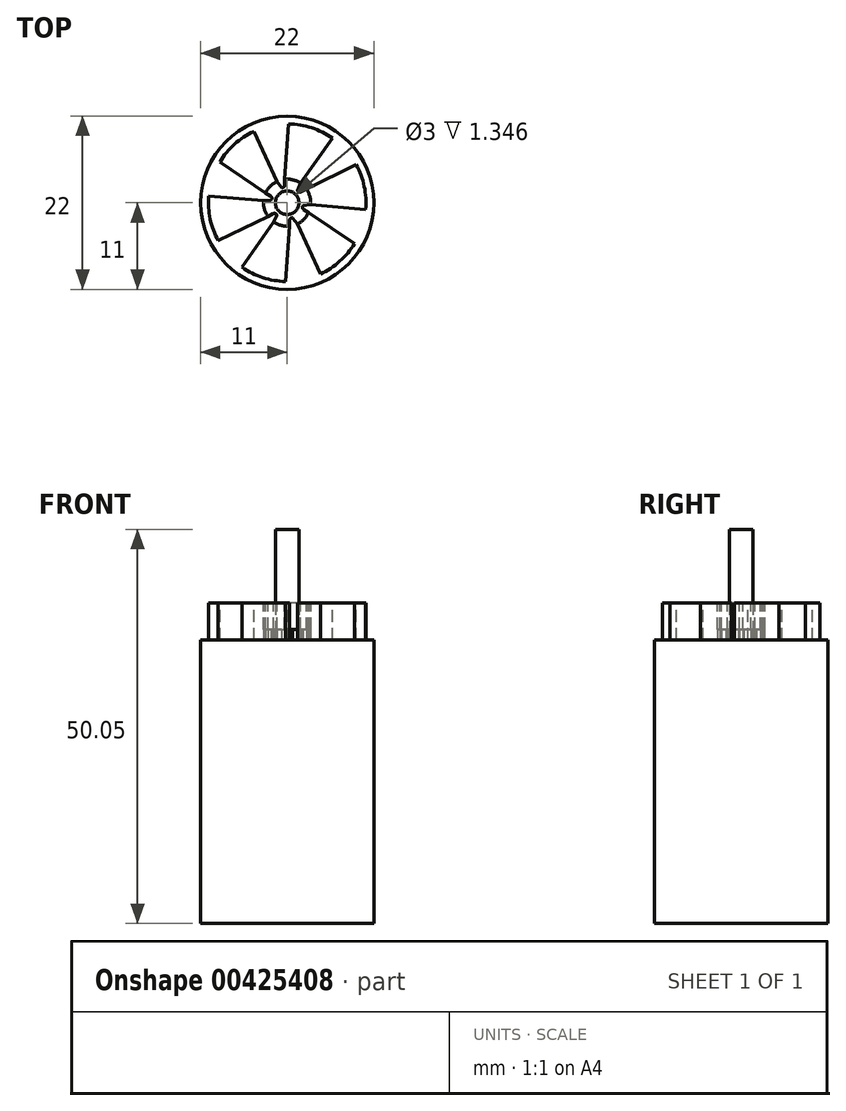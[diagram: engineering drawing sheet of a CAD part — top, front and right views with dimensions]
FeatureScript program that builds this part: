
annotation { "Feature Type Name" : "Feature", "Feature Type Description" : "" }
export const myFeature = defineFeature(function(context is Context, id is Id, definition is map)
    precondition{}
    {
        {
            var Q0;
            Q0=qCreatedBy(makeId("Top.planeOp"),FACE);
            var sketch = newSketch(context, id + "F0", { "sketchPlane" : qUnion([Q0])});
            skCircle(sketch, "E0", {"center": v(0, 0) * mm, "radius": 11 * mm});
            skSolve(sketch);
        }
        {
            var Q0;
            Q0=makeQuery(id+"F0.imprint","IMPRINT",FACE,{"disambiguationData":[TD([[makeQuery(id+"F0.imprint","IMPRINT",EDGE,{"derivedFrom":sQuery(id+"F0.wireOp",EDGE,"E0")}),1.0]])]});
            extrude(context, id + "F1", {"entities" : qUnion([Q0]), "depth" : 36 * mm});
        }
        {
            var Q0;
            Q0=makeQuery(id+"F1.opExtrude","CAP_FACE",FACE,{"disambiguationData":[OSD([sQuery(id+"F0.wireOp",EDGE,"E0")])],"isStart":false});
            var sketch = newSketch(context, id + "F2", { "sketchPlane" : qUnion([Q0])});
            skCircle(sketch, "E1", {"center": v(0, 0) * mm, "radius": 10 * mm});
            skCircle(sketch, "E2", {"center": v(0, 0) * mm, "radius": 1.5 * mm});
            skLineSegment(sketch, "E3", {"start": v(-0.3, 2.98) * mm, "end": v(-0.3, 2.25) * mm});
            skArc(sketch, "E4", {"start": v(-0.3, 2.25) * mm, "mid": v(-0.43, 2) * mm, "end": v(-0.7, 1.92) * mm});
            skLineSegment(sketch, "E5", {"start": v(-0.7, 1.92) * mm, "end": v(-1.29, 2.71) * mm});
            skLineSegment(sketch, "E6.1.0", {"start": v(-2.02, 0.35) * mm, "end": v(-3, 0.24) * mm});
            skArc(sketch, "E6.1.1", {"start": v(-2.1, 0.86) * mm, "mid": v(-1.94, 0.63) * mm, "end": v(-2.02, 0.35) * mm});
            skLineSegment(sketch, "E6.1.2", {"start": v(-2.74, 1.23) * mm, "end": v(-2.1, 0.86) * mm});
            skCircle(sketch, "E6.1.3", {"center": v(0, 0) * mm, "radius": 3 * mm});
            skLineSegment(sketch, "E6.2.0", {"start": v(-1.31, -1.57) * mm, "end": v(-1.7, -2.47) * mm});
            skArc(sketch, "E6.2.1", {"start": v(-1.8, -1.4) * mm, "mid": v(-1.51, -1.37) * mm, "end": v(-1.31, -1.57) * mm});
            skLineSegment(sketch, "E6.2.2", {"start": v(-2.43, -1.76) * mm, "end": v(-1.8, -1.4) * mm});
            skLineSegment(sketch, "E6.3.0", {"start": v(0.7, -1.92) * mm, "end": v(1.29, -2.71) * mm});
            skArc(sketch, "E6.3.1", {"start": v(0.3, -2.25) * mm, "mid": v(0.43, -2) * mm, "end": v(0.7, -1.92) * mm});
            skLineSegment(sketch, "E6.3.2", {"start": v(0.3, -2.98) * mm, "end": v(0.3, -2.25) * mm});
            skLineSegment(sketch, "E6.4.0", {"start": v(2.02, -0.35) * mm, "end": v(3, -0.24) * mm});
            skArc(sketch, "E6.4.1", {"start": v(2.1, -0.86) * mm, "mid": v(1.94, -0.63) * mm, "end": v(2.02, -0.35) * mm});
            skLineSegment(sketch, "E6.4.2", {"start": v(2.74, -1.23) * mm, "end": v(2.1, -0.86) * mm});
            skLineSegment(sketch, "E6.5.0", {"start": v(1.31, 1.57) * mm, "end": v(1.7, 2.47) * mm});
            skArc(sketch, "E6.5.1", {"start": v(1.8, 1.4) * mm, "mid": v(1.51, 1.37) * mm, "end": v(1.31, 1.57) * mm});
            skLineSegment(sketch, "E6.5.2", {"start": v(2.43, 1.76) * mm, "end": v(1.8, 1.4) * mm});
            skArc(sketch, "E7.trimOffspring", {"start": v(-2.43, -1.76) * mm, "mid": v(2.93, -0.63) * mm, "end": v(-1.5, 2.6) * mm});
            skSolve(sketch);
        }
        {
            var Q0;
            Q0=makeQuery(id+"F2.imprint","IMPRINT",FACE,{"disambiguationData":[TD([[makeQuery(id+"F2.imprint","IMPRINT",EDGE,{"derivedFrom":sQuery(id+"F2.wireOp",EDGE,"E2")}),-1.0]])]});
            extrude(context, id + "F3", {"entities" : qUnion([Q0]), "operationType" : NewBodyOperationType.ADD, "depth" : 1.35 * mm});
        }
        {
            var Q0;
            Q0=makeQuery(id+"F3.opExtrude","CAP_FACE",FACE,{"disambiguationData":[OSD([sQuery(id+"F2.wireOp",EDGE,"E2"),sQuery(id+"F2.wireOp",EDGE,"E3"),sQuery(id+"F2.wireOp",EDGE,"E4"),sQuery(id+"F2.wireOp",EDGE,"E5"),sQuery(id+"F2.wireOp",EDGE,"E6.1.0"),sQuery(id+"F2.wireOp",EDGE,"E6.1.1"),sQuery(id+"F2.wireOp",EDGE,"E6.1.2"),sQuery(id+"F2.wireOp",EDGE,"E6.1.3"),sQuery(id+"F2.wireOp",EDGE,"E6.2.0"),sQuery(id+"F2.wireOp",EDGE,"E6.2.1"),sQuery(id+"F2.wireOp",EDGE,"E6.2.2"),sQuery(id+"F2.wireOp",EDGE,"E6.3.0"),sQuery(id+"F2.wireOp",EDGE,"E6.3.1"),sQuery(id+"F2.wireOp",EDGE,"E6.3.2"),sQuery(id+"F2.wireOp",EDGE,"E6.4.0"),sQuery(id+"F2.wireOp",EDGE,"E6.4.1"),sQuery(id+"F2.wireOp",EDGE,"E6.4.2"),sQuery(id+"F2.wireOp",EDGE,"E6.5.0"),sQuery(id+"F2.wireOp",EDGE,"E6.5.1"),sQuery(id+"F2.wireOp",EDGE,"E6.5.2")])],"isStart":false});
            var sketch = newSketch(context, id + "F4", { "sketchPlane" : qUnion([Q0])});
            skSolve(sketch);
        }
        {
            var Q0;
            Q0=makeQuery(id+"F4.imprint","IMPRINT",FACE,{"disambiguationData":[TD([[makeQuery(id+"F4.imprint","IMPRINT",EDGE,{"derivedFrom":makeQuery(id+"F3.opExtrude","CAP_EDGE",EDGE,{"disambiguationData":[OSD([sQuery(id+"F2.wireOp",EDGE,"E2")])],"isStart":false})}),-1.0]])]});
            var sketch = newSketch(context, id + "F5", { "sketchPlane" : qUnion([Q0])});
            skCircle(sketch, "E8", {"center": v(0, 0) * mm, "radius": 1.5 * mm});
            skSolve(sketch);
        }
        {
            var Q0;
            Q0 = qSketchRegion(id + "F5", true);
            extrude(context, id + "F6", {"entities" : qUnion([Q0]), "operationType" : NewBodyOperationType.ADD, "depth" : 12.7 * mm});
        }
        {
            var Q0;
            {var subQ11=sQuery(id+"F0.wireOp",EDGE,"E0");Q0=makeQuery(id+"F3.boolean.opBoolean","SPLIT",FACE,{"disambiguationData":[TD([makeQuery(id+"F1.opExtrude","SWEPT_FACE",FACE,{"disambiguationData":[OSD([subQ11])]})])],"derivedFrom":makeQuery(id+"F1.opExtrude","CAP_FACE",FACE,{"disambiguationData":[OSD([subQ11])],"isStart":false})});}
            var sketch = newSketch(context, id + "F7", { "sketchPlane" : qUnion([Q0])});
            skCircle(sketch, "E9", {"center": v(0, 0) * mm, "radius": 10 * mm, "construction": true});
            skLineSegment(sketch, "E10", {"start": v(-1.29, 2.71) * mm, "end": v(-4.23, 9.06) * mm});
            skLineSegment(sketch, "E11", {"start": v(-2.74, 1.23) * mm, "end": v(-8.56, 5.17) * mm});
            skArc(sketch, "E12", {"start": v(-4.23, 9.06) * mm, "mid": v(-6.68, 7.44) * mm, "end": v(-8.56, 5.17) * mm});
            skLineSegment(sketch, "E13.1.0", {"start": v(-3, 0.24) * mm, "end": v(-9.96, 0.86) * mm});
            skArc(sketch, "E13.1.1", {"start": v(-8.56, 5.17) * mm, "mid": v(-9.5, 3.1) * mm, "end": v(-9.96, 0.86) * mm, "construction": true});
            skLineSegment(sketch, "E13.1.2", {"start": v(-2.43, -1.76) * mm, "end": v(-8.76, -4.82) * mm});
            skLineSegment(sketch, "E13.2.0", {"start": v(-1.7, -2.47) * mm, "end": v(-5.73, -8.2) * mm});
            skLineSegment(sketch, "E13.2.2", {"start": v(0.3, -2.98) * mm, "end": v(-0.2, -10) * mm});
            skLineSegment(sketch, "E13.3.0", {"start": v(1.29, -2.71) * mm, "end": v(4.23, -9.06) * mm});
            skLineSegment(sketch, "E13.3.2", {"start": v(2.74, -1.23) * mm, "end": v(8.56, -5.17) * mm});
            skLineSegment(sketch, "E13.4.0", {"start": v(3, -0.24) * mm, "end": v(9.96, -0.86) * mm});
            skLineSegment(sketch, "E13.4.2", {"start": v(2.43, 1.76) * mm, "end": v(8.76, 4.82) * mm});
            skLineSegment(sketch, "E13.5.0", {"start": v(1.7, 2.47) * mm, "end": v(5.73, 8.2) * mm});
            skLineSegment(sketch, "E13.5.2", {"start": v(-0.3, 2.98) * mm, "end": v(0.2, 10) * mm});
            skArc(sketch, "E14", {"start": v(5.73, 8.2) * mm, "mid": v(3.1, 9.52) * mm, "end": v(0.2, 10) * mm});
            skArc(sketch, "E15", {"start": v(9.96, -0.86) * mm, "mid": v(9.79, 2.07) * mm, "end": v(8.76, 4.82) * mm});
            skArc(sketch, "E16", {"start": v(4.23, -9.06) * mm, "mid": v(6.68, -7.44) * mm, "end": v(8.56, -5.17) * mm});
            skArc(sketch, "E17", {"start": v(-5.73, -8.2) * mm, "mid": v(-3.1, -9.51) * mm, "end": v(-0.2, -10) * mm});
            skArc(sketch, "E18", {"start": v(-9.96, 0.86) * mm, "mid": v(-9.78, -2.07) * mm, "end": v(-8.76, -4.82) * mm});
            skArc(sketch, "E19.trimOffspring", {"start": v(-5.73, -8.2) * mm, "mid": v(-3.1, -9.5) * mm, "end": v(-0.2, -10) * mm, "construction": true});
            skArc(sketch, "E20.trimOffspring", {"start": v(-8.76, -4.82) * mm, "mid": v(-5.17, -8.56) * mm, "end": v(-0.2, -10) * mm, "construction": true});
            skArc(sketch, "E21.trimOffspring", {"start": v(4.23, -9.06) * mm, "mid": v(6.68, -7.44) * mm, "end": v(8.56, -5.17) * mm, "construction": true});
            skArc(sketch, "E22.trimOffspring", {"start": v(9.96, -0.86) * mm, "mid": v(5.73, 8.2) * mm, "end": v(-4.23, 9.06) * mm, "construction": true});
            skArc(sketch, "E23.trimOffspring", {"start": v(5.73, 8.2) * mm, "mid": v(3.1, 9.5) * mm, "end": v(0.2, 10) * mm, "construction": true});
            skArc(sketch, "E24.trimOffspring", {"start": v(4.23, -9.06) * mm, "mid": v(9.5, -3.1) * mm, "end": v(8.76, 4.82) * mm, "construction": true});
            skSolve(sketch);
        }
        {
            var Q0;
            Q0=makeQuery(id+"F7.imprint","IMPRINT",FACE,{"disambiguationData":[TD([[makeQuery(id+"F7.imprint","IMPRINT",EDGE,{"derivedFrom":sQuery(id+"F7.wireOp",EDGE,"E13.1.0")}),1.0]])]});
            var Q1;
            Q1=makeQuery(id+"F7.imprint","IMPRINT",FACE,{"disambiguationData":[TD([[makeQuery(id+"F7.imprint","IMPRINT",EDGE,{"derivedFrom":sQuery(id+"F7.wireOp",EDGE,"E13.5.0")}),1.0]])]});
            var Q2;
            Q2=makeQuery(id+"F7.imprint","IMPRINT",FACE,{"disambiguationData":[TD([[makeQuery(id+"F7.imprint","IMPRINT",EDGE,{"derivedFrom":sQuery(id+"F7.wireOp",EDGE,"E13.4.0")}),1.0]])]});
            var Q3;
            Q3=makeQuery(id+"F7.imprint","IMPRINT",FACE,{"disambiguationData":[TD([[makeQuery(id+"F7.imprint","IMPRINT",EDGE,{"derivedFrom":sQuery(id+"F7.wireOp",EDGE,"E13.3.0")}),1.0]])]});
            var Q4;
            Q4=makeQuery(id+"F7.imprint","IMPRINT",FACE,{"disambiguationData":[TD([[makeQuery(id+"F7.imprint","IMPRINT",EDGE,{"derivedFrom":sQuery(id+"F7.wireOp",EDGE,"E10")}),1.0]])]});
            var Q5;
            Q5=makeQuery(id+"F7.imprint","IMPRINT",FACE,{"disambiguationData":[TD([[makeQuery(id+"F7.imprint","IMPRINT",EDGE,{"derivedFrom":sQuery(id+"F7.wireOp",EDGE,"E13.2.0")}),1.0]])]});
            extrude(context, id + "F8", {"entities" : qUnion([Q0, Q1, Q2, Q3, Q4, Q5]), "operationType" : NewBodyOperationType.ADD, "endBound" : BoundingType.SYMMETRIC, "oppositeDirection" : true, "depth" : 9.4 * mm});
        }
    });
